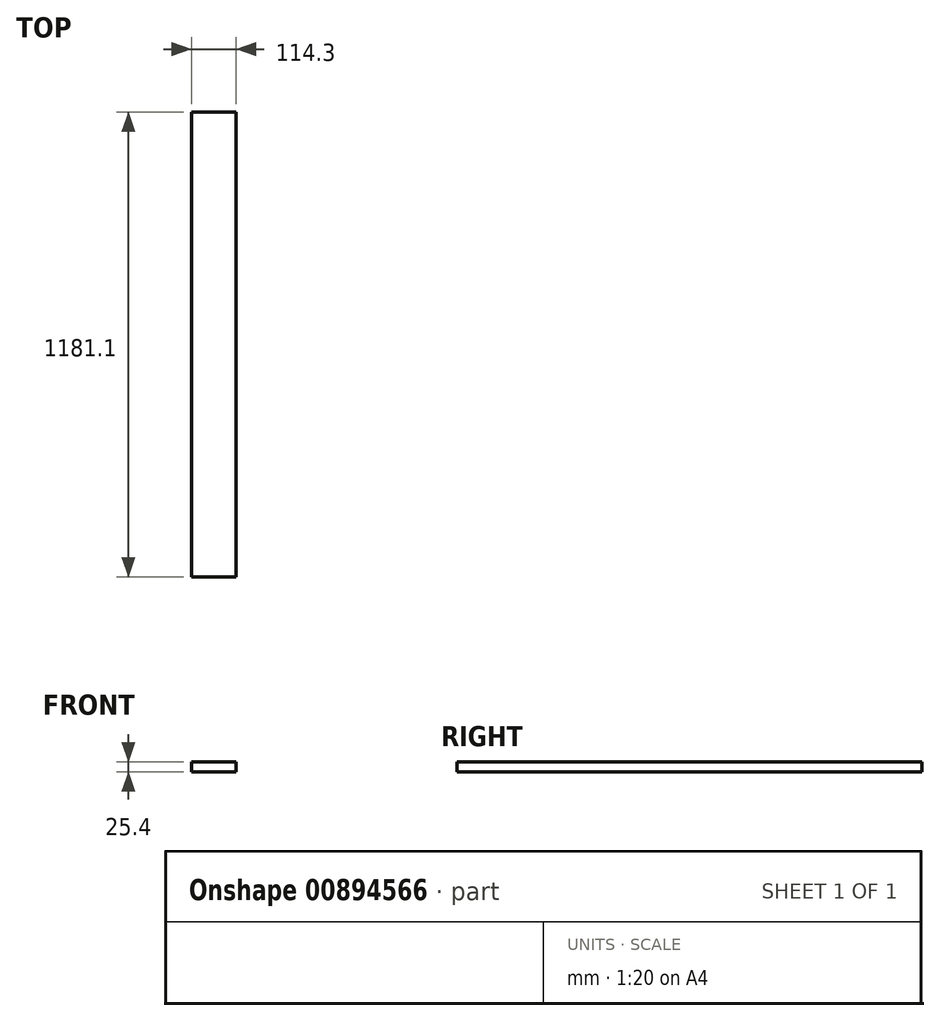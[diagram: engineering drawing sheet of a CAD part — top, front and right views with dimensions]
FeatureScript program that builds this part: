
annotation { "Feature Type Name" : "Feature", "Feature Type Description" : "" }
export const myFeature = defineFeature(function(context is Context, id is Id, definition is map)
    precondition{}
    {
        {
            var Q0;
            Q0=qCreatedBy(makeId("Top.planeOp"),FACE);
            var sketch = newSketch(context, id + "F0", { "sketchPlane" : qUnion([Q0])});
            skLineSegment(sketch, "E0.bottom", {"start": v(57.15, 590.55) * mm, "end": v(-57.15, 590.55) * mm});
            skLineSegment(sketch, "E0.top", {"start": v(57.15, -590.55) * mm, "end": v(-57.15, -590.55) * mm});
            skLineSegment(sketch, "E0.left", {"start": v(57.15, 590.55) * mm, "end": v(57.15, -590.55) * mm});
            skLineSegment(sketch, "E0.right", {"start": v(-57.15, 590.55) * mm, "end": v(-57.15, -590.55) * mm});
            skPoint(sketch, "E0.middle", {"position": v(0, 0) * mm});
            skSolve(sketch);
        }
        {
            var Q0;
            Q0=makeQuery(id+"F0.imprint","IMPRINT",FACE,{"disambiguationData":[TD([[makeQuery(id+"F0.imprint","IMPRINT",EDGE,{"derivedFrom":sQuery(id+"F0.wireOp",EDGE,"E0.bottom")}),1.0]])]});
            extrude(context, id + "F1", {"entities" : qUnion([Q0]), "depth" : 25.4 * mm, "offsetDistance" : 25.4 * mm});
        }
    });
